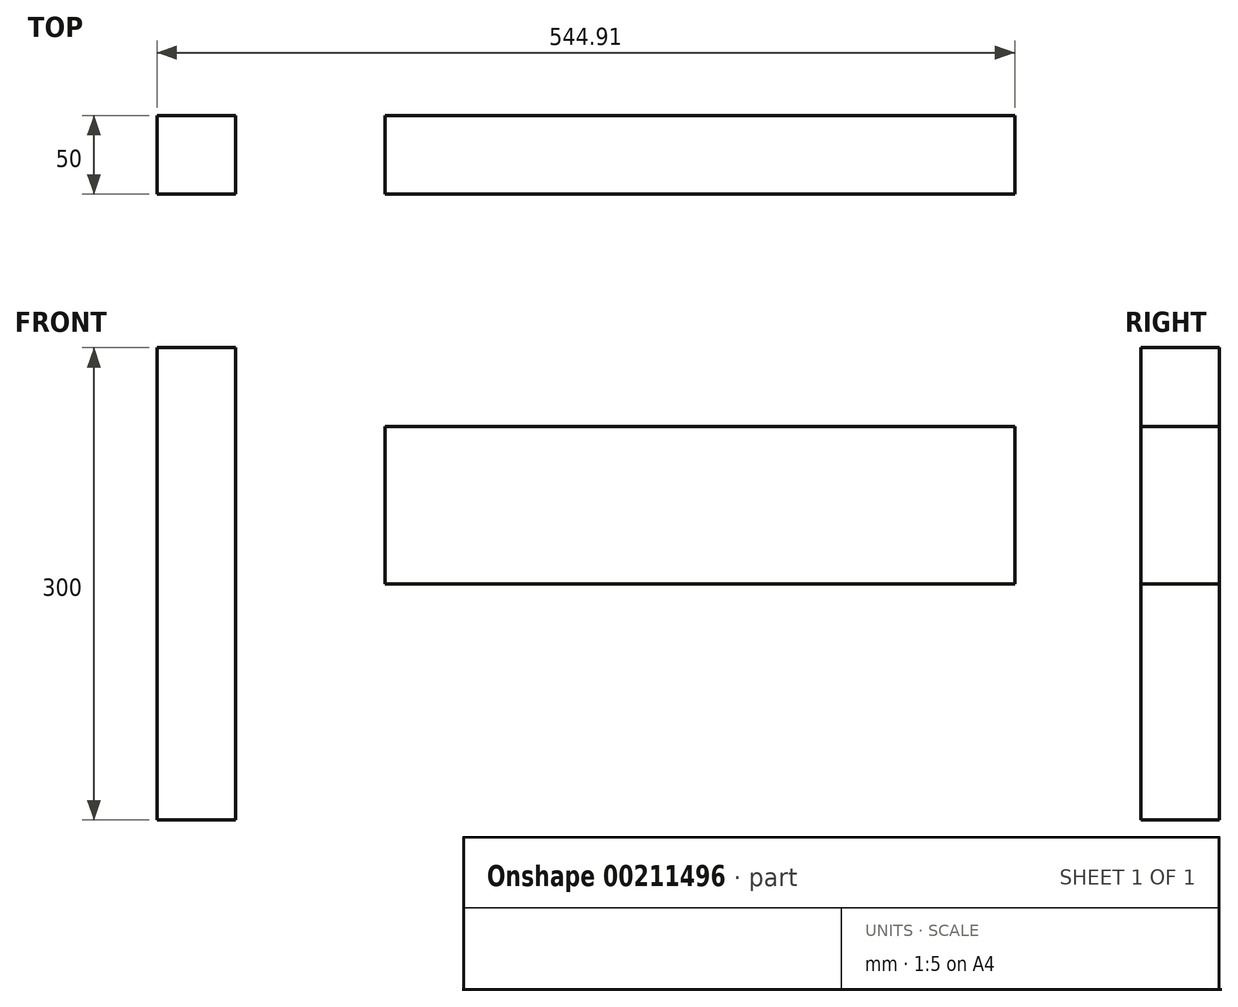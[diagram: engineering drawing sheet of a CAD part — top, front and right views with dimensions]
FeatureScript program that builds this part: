
annotation { "Feature Type Name" : "Feature", "Feature Type Description" : "" }
export const myFeature = defineFeature(function(context is Context, id is Id, definition is map)
    precondition{}
    {
        {
            var Q0;
            Q0=qCreatedBy(makeId("Top.planeOp"),FACE);
            var sketch = newSketch(context, id + "F0", { "sketchPlane" : qUnion([Q0])});
            skLineSegment(sketch, "E0.bottom", {"start": v(200, -25) * mm, "end": v(-200, -25) * mm});
            skLineSegment(sketch, "E0.top", {"start": v(200, 25) * mm, "end": v(-200, 25) * mm});
            skLineSegment(sketch, "E0.left", {"start": v(200, -25) * mm, "end": v(200, 25) * mm});
            skLineSegment(sketch, "E0.right", {"start": v(-200, -25) * mm, "end": v(-200, 25) * mm});
            skPoint(sketch, "E0.middle", {"position": v(0, 0) * mm});
            skSolve(sketch);
        }
        {
            var Q0;
            Q0=makeQuery(id+"F0.imprint","IMPRINT",FACE,{"disambiguationData":[TD([[makeQuery(id+"F0.imprint","IMPRINT",EDGE,{"derivedFrom":sQuery(id+"F0.wireOp",EDGE,"E0.bottom")}),-1.0]])]});
            extrude(context, id + "F1", {"entities" : qUnion([Q0]), "depth" : 25 * mm});
        }
        {
            var Q0;
            Q0 = qSketchRegion(id + "F0", true);
            extrude(context, id + "F2", {"entities" : qUnion([Q0]), "operationType" : NewBodyOperationType.ADD, "depth" : 100 * mm});
        }
        {
            var Q0;
            Q0=qCreatedBy(makeId("Top.planeOp"),FACE);
            var sketch = newSketch(context, id + "F3", { "sketchPlane" : qUnion([Q0])});
            skLineSegment(sketch, "E1.bottom", {"start": v(-294.9, -25) * mm, "end": v(-344.9, -25) * mm});
            skLineSegment(sketch, "E1.top", {"start": v(-294.9, 25) * mm, "end": v(-344.9, 25) * mm});
            skLineSegment(sketch, "E1.left", {"start": v(-294.9, -25) * mm, "end": v(-294.9, 25) * mm});
            skLineSegment(sketch, "E1.right", {"start": v(-344.9, -25) * mm, "end": v(-344.9, 25) * mm});
            skPoint(sketch, "E1.middle", {"position": v(-319.9, 0) * mm});
            skSolve(sketch);
        }
        {
            var Q0;
            Q0 = qSketchRegion(id + "F3", true);
            extrude(context, id + "F4", {"entities" : qUnion([Q0]), "depth" : 300 * mm});
        }
        {
            var Q0;
            Q0=makeQuery(id+"F4.opExtrude","SWEPT_BODY",BODY,{"disambiguationData":[OSD([sQuery(id+"F3.wireOp",EDGE,"E1.bottom"),sQuery(id+"F3.wireOp",EDGE,"E1.top"),sQuery(id+"F3.wireOp",EDGE,"E1.left"),sQuery(id+"F3.wireOp",EDGE,"E1.right")])]});
            var Q1;
            Q1=makeQuery(id+"F4.opExtrude","CAP_EDGE",EDGE,{"disambiguationData":[OSD([sQuery(id+"F3.wireOp",EDGE,"E1.top")])],"isStart":true});
            var Q2;
            Q2=makeQuery(id+"F4.opExtrude","CAP_VERTEX",VERTEX,{"disambiguationData":[OSD([sQuery(id+"F3.wireOp",EDGE,"E1.top"),sQuery(id+"F3.wireOp",EDGE,"E1.right")])],"isStart":true});
            transform(context, id + "F5", {"entities" : qUnion([Q0]), "transformType" : TransformType.TRANSLATION_3D, "dx" : 0 * mm, "dy" : 0 * mm, "dz" : -150 * mm, "makeCopy" : false});
        }
    });
